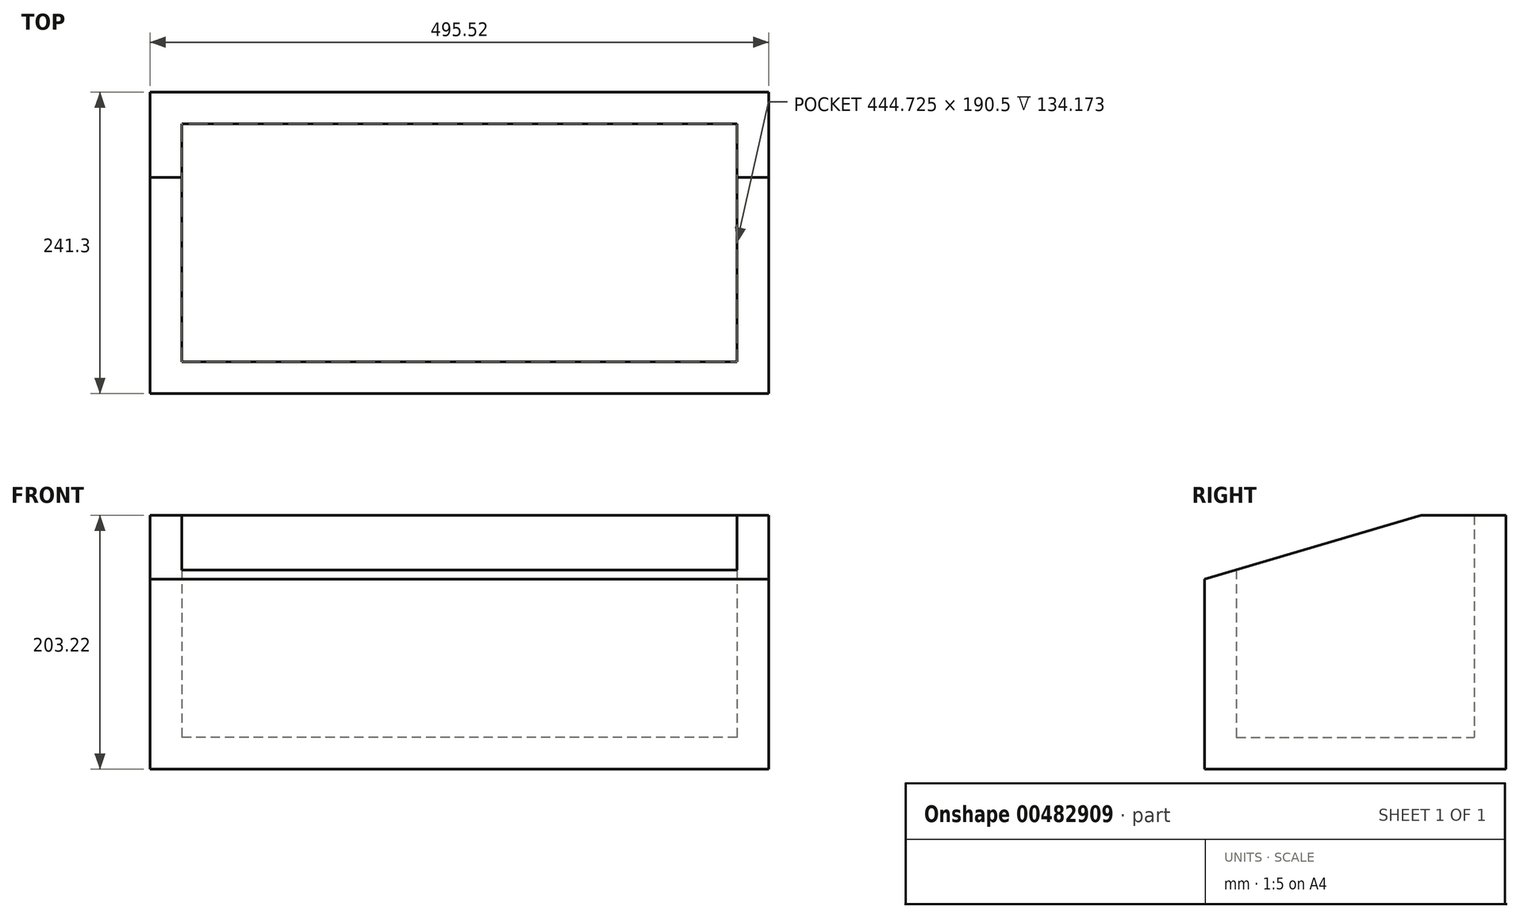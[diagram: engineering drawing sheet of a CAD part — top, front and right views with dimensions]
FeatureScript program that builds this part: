
annotation { "Feature Type Name" : "Feature", "Feature Type Description" : "" }
export const myFeature = defineFeature(function(context is Context, id is Id, definition is map)
    precondition{}
    {
        {
            var Q0;
            Q0=qCreatedBy(makeId("Front.planeOp"),FACE);
            var sketch = newSketch(context, id + "F0", { "sketchPlane" : qUnion([Q0])});
            skLineSegment(sketch, "E0.bottom", {"start": v(247.76, 101.6) * mm, "end": v(-247.76, 101.6) * mm});
            skLineSegment(sketch, "E0.top", {"start": v(247.76, -101.6) * mm, "end": v(-247.76, -101.6) * mm});
            skLineSegment(sketch, "E0.left", {"start": v(247.76, 101.6) * mm, "end": v(247.76, -101.6) * mm});
            skLineSegment(sketch, "E0.right", {"start": v(-247.76, 101.6) * mm, "end": v(-247.76, -101.6) * mm});
            skPoint(sketch, "E0.middle", {"position": v(0, 0) * mm});
            skSolve(sketch);
        }
        {
            var Q0;
            Q0 = qSketchRegion(id + "F0", true);
            extrude(context, id + "F1", {"entities" : qUnion([Q0]), "depth" : 241.3 * mm});
        }
        {
            var Q0;
            Q0=makeQuery(id+"F1.opExtrude","SWEPT_FACE",FACE,{"disambiguationData":[OSD([sQuery(id+"F0.wireOp",EDGE,"E0.bottom")])]});
            shell(context, id + "F2", {"entities" : qUnion([Q0]), "thickness" : 25.4 * mm});
        }
        {
            var Q0;
            Q0=makeQuery(id+"F1.opExtrude","SWEPT_FACE",FACE,{"disambiguationData":[OSD([sQuery(id+"F0.wireOp",EDGE,"E0.left")])]});
            var sketch = newSketch(context, id + "F3", { "sketchPlane" : qUnion([Q0])});
            skLineSegment(sketch, "E1", {"start": v(-241.3, 101.6) * mm, "end": v(-241.3, 50.47) * mm});
            skLineSegment(sketch, "E2", {"start": v(-241.3, 50.47) * mm, "end": v(-68.14, 101.6) * mm});
            skLineSegment(sketch, "E3", {"start": v(-68.14, 101.6) * mm, "end": v(-241.3, 101.6) * mm});
            skSolve(sketch);
        }
        {
            var Q0;
            Q0 = qSketchRegion(id + "F3", true);
            extrude(context, id + "F4", {"entities" : qUnion([Q0]), "operationType" : NewBodyOperationType.REMOVE, "oppositeDirection" : true, "depth" : 495.55 * mm});
        }
    });
